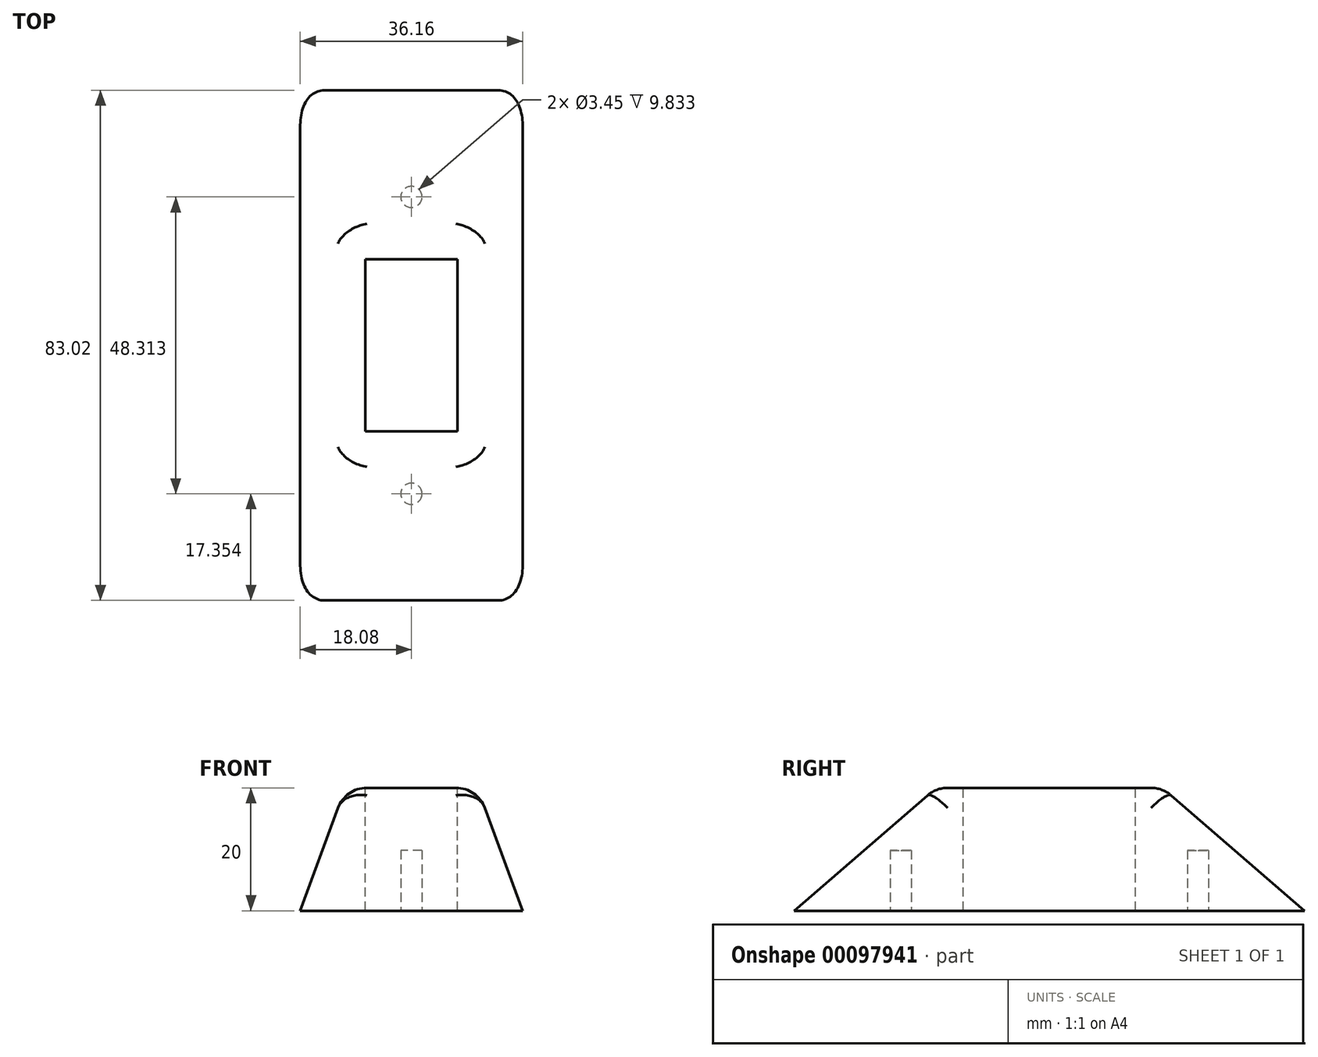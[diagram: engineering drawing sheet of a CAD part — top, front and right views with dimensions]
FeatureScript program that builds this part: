
annotation { "Feature Type Name" : "Feature", "Feature Type Description" : "" }
export const myFeature = defineFeature(function(context is Context, id is Id, definition is map)
    precondition{}
    {
        {
            var Q0;
            Q0=qCreatedBy(makeId("Top.planeOp"),FACE);
            var sketch = newSketch(context, id + "F0", { "sketchPlane" : qUnion([Q0])});
            skLineSegment(sketch, "E0", {"start": v(32.78, 28.12) * mm, "end": v(29.48, 28.12) * mm});
            skLineSegment(sketch, "E1", {"start": v(-13.66, -35.2) * mm, "end": v(-13.66, -38.5) * mm});
            skLineSegment(sketch, "E2", {"start": v(-32.24, -27.4) * mm, "end": v(-28.94, -27.4) * mm});
            skLineSegment(sketch, "E3", {"start": v(-28.94, -16.22) * mm, "end": v(-32.24, -16.22) * mm});
            skLineSegment(sketch, "E4", {"start": v(-28.94, 6) * mm, "end": v(-32.24, 6) * mm});
            skLineSegment(sketch, "E5", {"start": v(-32.24, 17.02) * mm, "end": v(-28.94, 17.02) * mm});
            skLineSegment(sketch, "E6", {"start": v(-28.94, 28.2) * mm, "end": v(-32.24, 28.2) * mm});
            skLineSegment(sketch, "E7", {"start": v(29.48, 16.94) * mm, "end": v(32.78, 16.94) * mm});
            skLineSegment(sketch, "E8", {"start": v(32.78, 5.92) * mm, "end": v(29.48, 5.92) * mm});
            skLineSegment(sketch, "E9", {"start": v(29.48, -27.47) * mm, "end": v(32.78, -27.47) * mm});
            skLineSegment(sketch, "E10", {"start": v(-13.74, 39.23) * mm, "end": v(-13.74, 35.93) * mm});
            skLineSegment(sketch, "E11", {"start": v(-28.94, -35.2) * mm, "end": v(-28.94, -38.5) * mm});
            skLineSegment(sketch, "E12", {"start": v(-32.24, -5.19) * mm, "end": v(-28.94, -5.19) * mm});
            skLineSegment(sketch, "E13", {"start": v(29.48, -5.26) * mm, "end": v(32.78, -5.26) * mm});
            skLineSegment(sketch, "E14", {"start": v(-22.88, -38.5) * mm, "end": v(-22.88, -35.2) * mm});
            skLineSegment(sketch, "E15", {"start": v(-4.3, -38.5) * mm, "end": v(-4.3, -35.2) * mm});
            skLineSegment(sketch, "E16", {"start": v(4.91, -35.2) * mm, "end": v(4.91, -38.5) * mm});
            skLineSegment(sketch, "E17", {"start": v(14.28, -38.5) * mm, "end": v(14.28, -35.2) * mm});
            skLineSegment(sketch, "E18", {"start": v(23.5, -35.2) * mm, "end": v(23.5, -38.5) * mm});
            skLineSegment(sketch, "E19", {"start": v(29.48, -38.5) * mm, "end": v(29.48, -35.2) * mm});
            skLineSegment(sketch, "E20", {"start": v(29.48, 35.93) * mm, "end": v(29.48, 39.23) * mm});
            skLineSegment(sketch, "E21", {"start": v(23.42, 39.23) * mm, "end": v(23.42, 35.93) * mm});
            skLineSegment(sketch, "E22", {"start": v(14.2, 35.93) * mm, "end": v(14.2, 39.23) * mm});
            skLineSegment(sketch, "E23", {"start": v(4.84, 39.23) * mm, "end": v(4.84, 35.93) * mm});
            skLineSegment(sketch, "E24", {"start": v(32.78, -16.3) * mm, "end": v(29.48, -16.3) * mm});
            skLineSegment(sketch, "E25", {"start": v(-4.37, 35.93) * mm, "end": v(-4.37, 39.23) * mm});
            skLineSegment(sketch, "E26", {"start": v(-22.95, 35.93) * mm, "end": v(-22.95, 39.23) * mm});
            skLineSegment(sketch, "E27", {"start": v(-28.94, 39.23) * mm, "end": v(-28.94, 35.93) * mm});
            skLineSegment(sketch, "E28", {"start": v(-32.24, 39.23) * mm, "end": v(-28.94, 39.23) * mm});
            skLineSegment(sketch, "E29", {"start": v(23.5, -38.5) * mm, "end": v(14.28, -38.5) * mm});
            skLineSegment(sketch, "E30", {"start": v(-32.24, 6) * mm, "end": v(-32.24, 17.02) * mm});
            skLineSegment(sketch, "E31", {"start": v(32.78, -27.47) * mm, "end": v(32.78, -38.5) * mm});
            skLineSegment(sketch, "E32", {"start": v(29.48, -38.5) * mm, "end": v(32.78, -38.5) * mm});
            skLineSegment(sketch, "E33.bottom", {"start": v(36.12, 48.67) * mm, "end": v(11.08, 48.67) * mm});
            skLineSegment(sketch, "E33.top", {"start": v(36.12, -48.67) * mm, "end": v(11.08, -48.67) * mm});
            skLineSegment(sketch, "E33.left", {"start": v(41.12, 43.67) * mm, "end": v(41.12, -43.67) * mm});
            skLineSegment(sketch, "E33.right", {"start": v(-41.12, 43.67) * mm, "end": v(-41.12, -43.67) * mm});
            skPoint(sketch, "E33.middle", {"position": v(0, 0) * mm});
            skPoint(sketch, "E34.visualSharp", {"position": v(-41.12, 48.67) * mm});
            skArc(sketch, "E34.filletArc", {"start": v(-36.12, 48.67) * mm, "mid": v(-39.66, 47.2) * mm, "end": v(-41.12, 43.67) * mm});
            skPoint(sketch, "E35.visualSharp", {"position": v(41.12, 48.67) * mm});
            skArc(sketch, "E35.filletArc", {"start": v(41.12, 43.67) * mm, "mid": v(39.66, 47.2) * mm, "end": v(36.12, 48.67) * mm});
            skPoint(sketch, "E36.visualSharp", {"position": v(41.12, -48.67) * mm});
            skArc(sketch, "E36.filletArc", {"start": v(36.12, -48.67) * mm, "mid": v(39.66, -47.2) * mm, "end": v(41.12, -43.67) * mm});
            skPoint(sketch, "E37.visualSharp", {"position": v(-41.12, -48.67) * mm});
            skArc(sketch, "E37.filletArc", {"start": v(-41.12, -43.67) * mm, "mid": v(-39.66, -47.2) * mm, "end": v(-36.12, -48.67) * mm});
            skLineSegment(sketch, "E38.trimOffspring", {"start": v(-4.37, 39.23) * mm, "end": v(4.84, 39.23) * mm});
            skLineSegment(sketch, "E39.trimOffspring", {"start": v(14.2, 39.23) * mm, "end": v(23.42, 39.23) * mm});
            skLineSegment(sketch, "E40.trimOffspring", {"start": v(-13.66, -38.5) * mm, "end": v(-22.88, -38.5) * mm});
            skLineSegment(sketch, "E41.trimOffspring", {"start": v(4.91, -38.5) * mm, "end": v(-4.3, -38.5) * mm});
            skLineSegment(sketch, "E42.trimOffspring", {"start": v(-28.94, -38.5) * mm, "end": v(-32.24, -38.5) * mm});
            skLineSegment(sketch, "E43.trimOffspring", {"start": v(-32.24, -27.4) * mm, "end": v(-32.24, -38.5) * mm});
            skLineSegment(sketch, "E44.trimOffspring", {"start": v(-32.24, 28.2) * mm, "end": v(-32.24, 39.23) * mm});
            skLineSegment(sketch, "E45.trimOffspring", {"start": v(-22.95, 39.23) * mm, "end": v(-13.74, 39.23) * mm});
            skLineSegment(sketch, "E46.trimOffspring", {"start": v(29.48, 39.23) * mm, "end": v(32.78, 39.23) * mm});
            skLineSegment(sketch, "E47.trimOffspring", {"start": v(32.78, 28.12) * mm, "end": v(32.78, 39.23) * mm});
            skLineSegment(sketch, "E48.trimOffspring", {"start": v(32.78, 5.92) * mm, "end": v(32.78, 16.94) * mm});
            skLineSegment(sketch, "E49", {"start": v(-32.24, -5.19) * mm, "end": v(-32.24, -16.22) * mm});
            skLineSegment(sketch, "E50", {"start": v(32.78, -5.26) * mm, "end": v(32.78, -16.3) * mm});
            skLineSegment(sketch, "E51", {"start": v(-28.94, 28.2) * mm, "end": v(-28.94, 17.02) * mm});
            skLineSegment(sketch, "E52", {"start": v(-28.94, 6) * mm, "end": v(-28.94, -5.19) * mm});
            skLineSegment(sketch, "E53", {"start": v(-28.94, -16.22) * mm, "end": v(-28.94, -27.4) * mm});
            skLineSegment(sketch, "E54", {"start": v(29.48, 28.12) * mm, "end": v(29.48, 16.94) * mm});
            skLineSegment(sketch, "E55", {"start": v(29.48, 5.92) * mm, "end": v(29.48, -5.26) * mm});
            skLineSegment(sketch, "E56", {"start": v(29.58, -16.3) * mm, "end": v(29.48, -27.47) * mm});
            skLineSegment(sketch, "E57", {"start": v(-13.74, 35.93) * mm, "end": v(-4.37, 35.93) * mm});
            skLineSegment(sketch, "E58", {"start": v(4.84, 35.93) * mm, "end": v(14.2, 35.93) * mm});
            skLineSegment(sketch, "E59", {"start": v(-22.95, 35.93) * mm, "end": v(-28.94, 35.93) * mm});
            skLineSegment(sketch, "E60", {"start": v(23.42, 35.93) * mm, "end": v(29.48, 35.93) * mm});
            skLineSegment(sketch, "E61", {"start": v(-13.66, -35.2) * mm, "end": v(-4.3, -35.2) * mm});
            skLineSegment(sketch, "E62", {"start": v(4.91, -35.2) * mm, "end": v(14.28, -35.2) * mm});
            skLineSegment(sketch, "E63", {"start": v(23.5, -35.2) * mm, "end": v(29.48, -35.2) * mm});
            skLineSegment(sketch, "E64", {"start": v(-22.88, -35.2) * mm, "end": v(-28.94, -35.2) * mm});
            skCircle(sketch, "E65", {"center": v(0, 52.98) * mm, "radius": 3.18 * mm});
            skArc(sketch, "E66", {"start": v(6.05, 53.66) * mm, "mid": v(0, 59.07) * mm, "end": v(-6.05, 53.66) * mm});
            skLineSegment(sketch, "E67", {"start": v(6.11, 53.1) * mm, "end": v(6.05, 53.66) * mm});
            skArc(sketch, "E68.filletArc", {"start": v(6.11, 53.1) * mm, "mid": v(7.75, 49.94) * mm, "end": v(11.08, 48.67) * mm});
            skLineSegment(sketch, "E69.MirrorCS", {"start": v(-6.11, 53.1) * mm, "end": v(-6.05, 53.66) * mm});
            skArc(sketch, "E70.MirrorCS", {"start": v(-6.11, 53.1) * mm, "mid": v(-7.75, 49.94) * mm, "end": v(-11.08, 48.67) * mm});
            skLineSegment(sketch, "E71.MirrorCS", {"start": v(-36.12, 48.67) * mm, "end": v(-11.08, 48.67) * mm});
            skCircle(sketch, "E72.MirrorC", {"center": v(0, -52.98) * mm, "radius": 3.18 * mm});
            skArc(sketch, "E73.MirrorCS", {"start": v(6.05, -53.66) * mm, "mid": v(0, -59.07) * mm, "end": v(-6.05, -53.66) * mm});
            skArc(sketch, "E74.MirrorCS", {"start": v(6.11, -53.1) * mm, "mid": v(7.75, -49.94) * mm, "end": v(11.08, -48.67) * mm});
            skArc(sketch, "E75.MirrorCS", {"start": v(-6.11, -53.1) * mm, "mid": v(-7.75, -49.94) * mm, "end": v(-11.08, -48.67) * mm});
            skLineSegment(sketch, "E76.trimOffspring", {"start": v(-11.08, -48.67) * mm, "end": v(-36.12, -48.67) * mm});
            skLineSegment(sketch, "E77.MirrorCS", {"start": v(-6.11, -53.1) * mm, "end": v(-6.05, -53.66) * mm});
            skLineSegment(sketch, "E78.MirrorCS", {"start": v(6.11, -53.1) * mm, "end": v(6.05, -53.66) * mm});
            skSolve(sketch);
        }
        {
            var Q0;
            Q0=qCreatedBy(makeId("Top.planeOp"),FACE);
            var sketch = newSketch(context, id + "F1", { "sketchPlane" : qUnion([Q0])});
            skLineSegment(sketch, "E79.0", {"start": v(-36.12, 48.67) * mm, "end": v(-11.08, 48.67) * mm});
            skArc(sketch, "E80.0", {"start": v(-36.12, 48.67) * mm, "mid": v(-39.66, 47.2) * mm, "end": v(-41.12, 43.67) * mm});
            skLineSegment(sketch, "E81.0", {"start": v(-41.12, 43.67) * mm, "end": v(-41.12, -43.67) * mm});
            skArc(sketch, "E82.0", {"start": v(-41.12, -43.67) * mm, "mid": v(-39.66, -47.2) * mm, "end": v(-36.12, -48.67) * mm});
            skLineSegment(sketch, "E83.0", {"start": v(-11.08, -48.67) * mm, "end": v(-36.12, -48.67) * mm});
            skArc(sketch, "E84.0", {"start": v(-6.11, -53.1) * mm, "mid": v(-7.75, -49.94) * mm, "end": v(-11.08, -48.67) * mm});
            skLineSegment(sketch, "E85.0", {"start": v(-6.11, -53.1) * mm, "end": v(-6.05, -53.66) * mm});
            skArc(sketch, "E86.0", {"start": v(6.05, -53.66) * mm, "mid": v(0, -59.07) * mm, "end": v(-6.05, -53.66) * mm});
            skLineSegment(sketch, "E87.0", {"start": v(6.11, -53.1) * mm, "end": v(6.05, -53.66) * mm});
            skArc(sketch, "E88.0", {"start": v(6.11, -53.1) * mm, "mid": v(7.75, -49.94) * mm, "end": v(11.08, -48.67) * mm});
            skLineSegment(sketch, "E89.0", {"start": v(36.12, -48.67) * mm, "end": v(11.08, -48.67) * mm});
            skArc(sketch, "E90.0", {"start": v(36.12, -48.67) * mm, "mid": v(39.66, -47.2) * mm, "end": v(41.12, -43.67) * mm});
            skLineSegment(sketch, "E91.0", {"start": v(41.12, 43.67) * mm, "end": v(41.12, -43.67) * mm});
            skArc(sketch, "E92.0", {"start": v(41.12, 43.67) * mm, "mid": v(39.66, 47.2) * mm, "end": v(36.12, 48.67) * mm});
            skLineSegment(sketch, "E93.0", {"start": v(36.12, 48.67) * mm, "end": v(11.08, 48.67) * mm});
            skArc(sketch, "E94.0", {"start": v(6.11, 53.1) * mm, "mid": v(7.75, 49.94) * mm, "end": v(11.08, 48.67) * mm});
            skArc(sketch, "E95.0", {"start": v(-6.11, 53.1) * mm, "mid": v(-7.75, 49.94) * mm, "end": v(-11.08, 48.67) * mm});
            skLineSegment(sketch, "E96.0", {"start": v(-6.11, 53.1) * mm, "end": v(-6.05, 53.66) * mm});
            skArc(sketch, "E97.0", {"start": v(6.05, 53.66) * mm, "mid": v(0, 59.07) * mm, "end": v(-6.05, 53.66) * mm});
            skLineSegment(sketch, "E98.0", {"start": v(6.11, 53.1) * mm, "end": v(6.05, 53.66) * mm});
            skLineSegment(sketch, "E99.bottom", {"start": v(7.5, -14) * mm, "end": v(-7.5, -14) * mm});
            skLineSegment(sketch, "E99.top", {"start": v(7.5, 14) * mm, "end": v(-7.5, 14) * mm});
            skLineSegment(sketch, "E99.left", {"start": v(7.5, -14) * mm, "end": v(7.5, 14) * mm});
            skLineSegment(sketch, "E99.right", {"start": v(-7.5, -14) * mm, "end": v(-7.5, 14) * mm});
            skPoint(sketch, "E99.middle", {"position": v(0, 0) * mm});
            skCircle(sketch, "E100", {"center": v(0, 24.16) * mm, "radius": 2.16 * mm});
            skCircle(sketch, "E101.MirrorC", {"center": v(0, -24.16) * mm, "radius": 2.16 * mm});
            skCircle(sketch, "E102.0", {"center": v(0, 52.98) * mm, "radius": 3.18 * mm});
            skCircle(sketch, "E103.0", {"center": v(0, -52.98) * mm, "radius": 3.18 * mm});
            skSolve(sketch);
        }
        {
            var Q0;
            Q0=qCreatedBy(makeId("Top.planeOp"),FACE);
            cPlane(context, id + "F2", {"entities" : qUnion([Q0]), "cplaneType" : CPlaneType.OFFSET, "offset" : 20 * mm, "width" : 150 * mm, "height" : 150 * mm});
        }
        {
            var Q0;
            Q0=qCreatedBy(id+"F2.planeOp",FACE);
            var sketch = newSketch(context, id + "F3", { "sketchPlane" : qUnion([Q0])});
            skLineSegment(sketch, "E104.bottom", {"start": v(10.74, 18.38) * mm, "end": v(-10.74, 18.38) * mm});
            skLineSegment(sketch, "E104.top", {"start": v(10.74, -18.38) * mm, "end": v(-10.74, -18.38) * mm});
            skLineSegment(sketch, "E104.left", {"start": v(10.74, 18.38) * mm, "end": v(10.74, -18.38) * mm});
            skLineSegment(sketch, "E104.right", {"start": v(-10.74, 18.38) * mm, "end": v(-10.74, -18.38) * mm});
            skPoint(sketch, "E104.middle", {"position": v(0, 0) * mm});
            skSolve(sketch);
        }
        {
            var Q0;
            Q0=qCreatedBy(makeId("Top.planeOp"),FACE);
            var sketch = newSketch(context, id + "F4", { "sketchPlane" : qUnion([Q0])});
            skLineSegment(sketch, "E105.bottom", {"start": v(18.08, 41.5) * mm, "end": v(-18.08, 41.5) * mm});
            skLineSegment(sketch, "E105.top", {"start": v(18.08, -41.5) * mm, "end": v(-18.08, -41.5) * mm});
            skLineSegment(sketch, "E105.left", {"start": v(18.08, 41.5) * mm, "end": v(18.08, -41.5) * mm});
            skLineSegment(sketch, "E105.right", {"start": v(-18.08, 41.5) * mm, "end": v(-18.08, -41.5) * mm});
            skPoint(sketch, "E105.middle", {"position": v(0, 0) * mm});
            skSolve(sketch);
        }
        {
            var Q0;
            Q0=makeQuery(id+"F3.imprint","IMPRINT",FACE,{"disambiguationData":[TD([[makeQuery(id+"F3.imprint","IMPRINT",EDGE,{"derivedFrom":sQuery(id+"F3.wireOp",EDGE,"E104.bottom")}),1.0]])]});
            var Q1;
            Q1=makeQuery(id+"F4.imprint","IMPRINT",FACE,{"disambiguationData":[TD([[makeQuery(id+"F4.imprint","IMPRINT",EDGE,{"derivedFrom":sQuery(id+"F4.wireOp",EDGE,"E105.bottom")}),1.0]])]});
            loft(context, id + "F5", {"sheetProfilesArray" : [{ "sheetProfileEntities" : qUnion([Q0]) }, { "sheetProfileEntities" : qUnion([Q1]) }]});
        }
        {
            var Q0;
            Q0=makeQuery(id+"F5.opLoft","CAP_FACE",FACE,{"disambiguationData":[OSD([makeQuery(id+"F3.imprint","IMPRINT",FACE,{"disambiguationData":[TD([[makeQuery(id+"F3.imprint","IMPRINT",EDGE,{"derivedFrom":sQuery(id+"F3.wireOp",EDGE,"E104.bottom")}),1.0]])]})])],"isStart":true});
            var sketch = newSketch(context, id + "F6", { "sketchPlane" : qUnion([Q0])});
            skLineSegment(sketch, "E106.0", {"start": v(7.5, -14) * mm, "end": v(7.5, 14) * mm});
            skLineSegment(sketch, "E107.0", {"start": v(7.5, -14) * mm, "end": v(-7.5, -14) * mm});
            skLineSegment(sketch, "E108.0", {"start": v(-7.5, -14) * mm, "end": v(-7.5, 14) * mm});
            skLineSegment(sketch, "E109.0", {"start": v(7.5, 14) * mm, "end": v(-7.5, 14) * mm});
            skSolve(sketch);
        }
        {
            var Q0;
            Q0 = qSketchRegion(id + "F6", true);
            extrude(context, id + "F7", {"entities" : qUnion([Q0]), "operationType" : NewBodyOperationType.REMOVE, "oppositeDirection" : true, "depth" : 25 * mm});
        }
        {
            var Q0;
            Q0=makeQuery(id+"F0.imprint","IMPRINT",FACE,{"disambiguationData":[TD([[makeQuery(id+"F0.imprint","IMPRINT",EDGE,{"derivedFrom":sQuery(id+"F0.wireOp",EDGE,"E33.bottom")}),1.0]])]});
            var sketch = newSketch(context, id + "F8", { "sketchPlane" : qUnion([Q0])});
            skCircle(sketch, "E110", {"center": v(0, 24.16) * mm, "radius": 1.73 * mm});
            skCircle(sketch, "E111.MirrorC", {"center": v(0, -24.16) * mm, "radius": 1.73 * mm});
            skSolve(sketch);
        }
        {
            var Q0;
            Q0 = qSketchRegion(id + "F8", true);
            extrude(context, id + "F9", {"entities" : qUnion([Q0]), "operationType" : NewBodyOperationType.REMOVE, "depth" : 9.83 * mm});
        }
        {
            var Q0;
            Q0=makeQuery(id+"F5.opLoft","SWEPT_EDGE",EDGE,{"disambiguationData":[OSD([sQuery(id+"F3.wireOp",EDGE,"E104.top"),sQuery(id+"F3.wireOp",EDGE,"E104.left"),sQuery(id+"F4.wireOp",EDGE,"E105.top"),sQuery(id+"F4.wireOp",EDGE,"E105.left")])]});
            var Q1;
            Q1=makeQuery(id+"F5.opLoft","SWEPT_EDGE",EDGE,{"disambiguationData":[OSD([sQuery(id+"F3.wireOp",EDGE,"E104.top"),sQuery(id+"F3.wireOp",EDGE,"E104.right"),sQuery(id+"F4.wireOp",EDGE,"E105.top"),sQuery(id+"F4.wireOp",EDGE,"E105.right")])]});
            var Q2;
            Q2=makeQuery(id+"F5.opLoft","SWEPT_EDGE",EDGE,{"disambiguationData":[OSD([sQuery(id+"F3.wireOp",EDGE,"E104.bottom"),sQuery(id+"F3.wireOp",EDGE,"E104.right"),sQuery(id+"F4.wireOp",EDGE,"E105.bottom"),sQuery(id+"F4.wireOp",EDGE,"E105.right")])]});
            var Q3;
            Q3=makeQuery(id+"F5.opLoft","SWEPT_EDGE",EDGE,{"disambiguationData":[OSD([sQuery(id+"F3.wireOp",EDGE,"E104.bottom"),sQuery(id+"F3.wireOp",EDGE,"E104.left"),sQuery(id+"F4.wireOp",EDGE,"E105.bottom"),sQuery(id+"F4.wireOp",EDGE,"E105.left")])]});
            fillet(context, id + "F10", {"entities" : qUnion([Q0, Q1, Q2, Q3]), "radius" : 5 * mm, "tangentPropagation" : true, "allowEdgeOverflow" : false});
        }
        {
            var Q0;
            Q0=makeQuery(id+"F5.opLoft","MID_CAP_EDGE",EDGE,{"disambiguationData":[OSD([sQuery(id+"F3.wireOp",EDGE,"E104.top"),sQuery(id+"F3.wireOp",EDGE,"E104.left"),sQuery(id+"F3.wireOp",EDGE,"E104.right")])],"capPos":0.0});
            fillet(context, id + "F11", {"entities" : qUnion([Q0]), "radius" : 5 * mm, "tangentPropagation" : true, "allowEdgeOverflow" : false});
        }
    });
